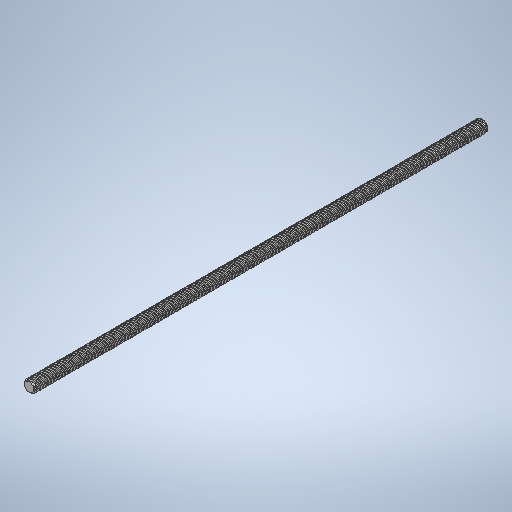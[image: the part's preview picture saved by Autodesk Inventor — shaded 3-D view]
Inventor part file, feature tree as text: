
AUTODESK INVENTOR PART (.ipt)
format: ipt  version: 2025.2 (Build 292293000, 293)  size: 1,358,336 bytes
history: native  units: mm
features: extrude x1, chamfer x1, other x1, pattern_circular x1
ambient origin geometry x8: Origin, YZ Plane, XZ Plane, XY Plane, X Axis, Y Axis, Z Axis, Center Point
bodies: Solid1 (feature_tree)
feature tree (4):
  extrude  "1000mm Rod"  Depth=300.0mm TaperAngle=0.0deg
  chamfer  "Chamfer1"  Distance=0.907143mm Angle=45.0deg
  other  "ACME Thread 2mm Pitch"
  pattern_circular  "4 Start"  [2 undecoded]
note: 2 required parameter values undecoded (feature->parameter linkage not recoverable at this tier; creation-order binding heuristic only, values carry confidence <= 0.55)
